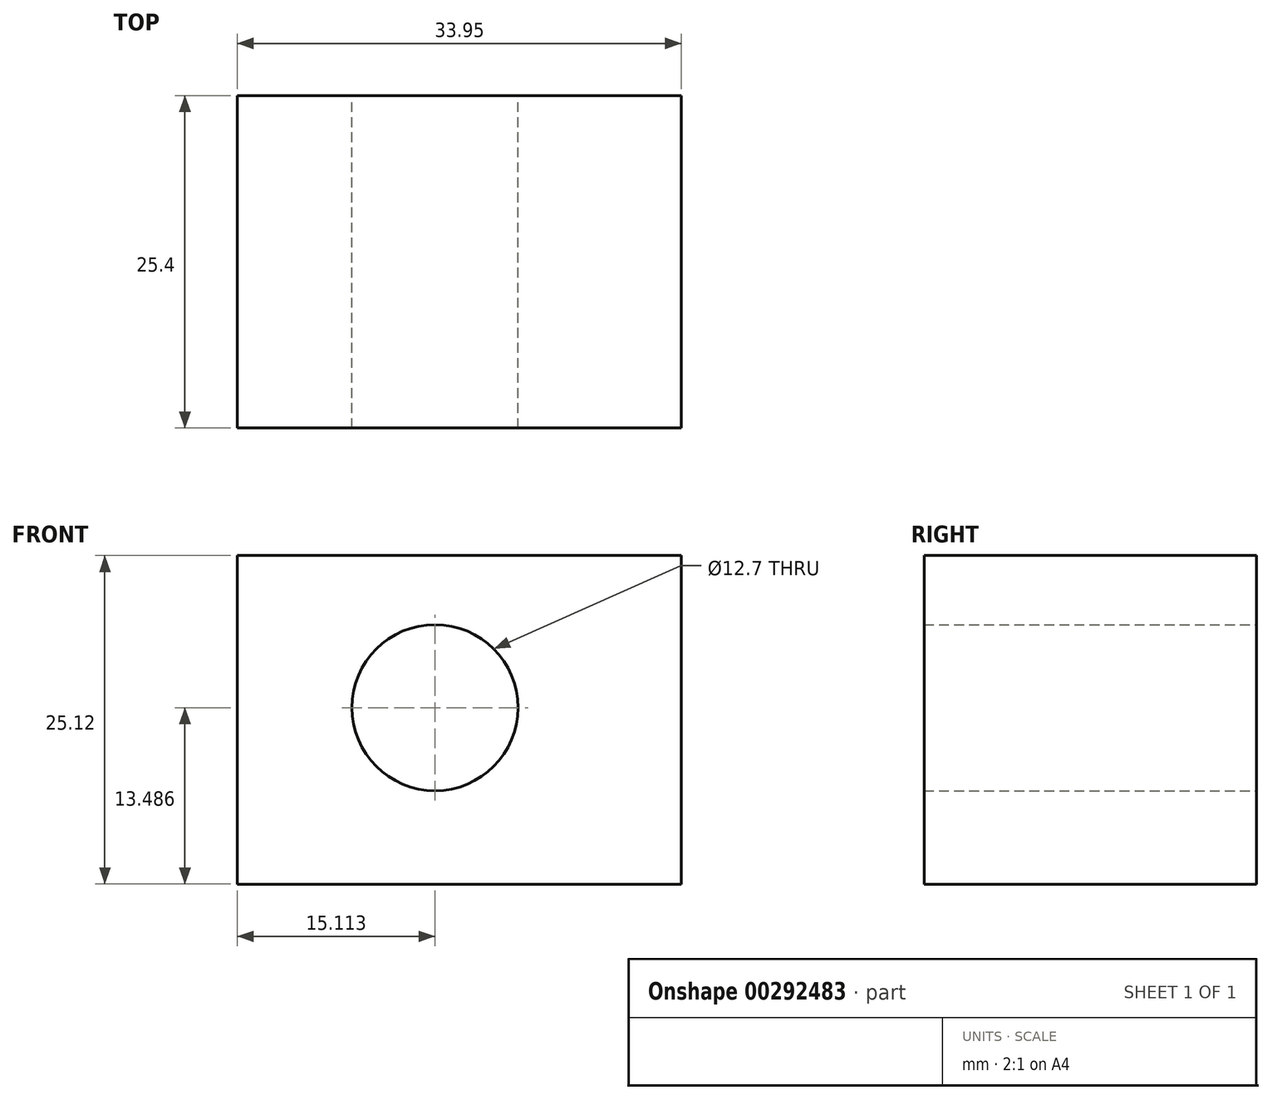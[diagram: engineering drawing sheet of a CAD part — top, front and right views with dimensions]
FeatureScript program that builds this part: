
annotation { "Feature Type Name" : "Feature", "Feature Type Description" : "" }
export const myFeature = defineFeature(function(context is Context, id is Id, definition is map)
    precondition{}
    {
        {
            var Q0;
            Q0=qCreatedBy(makeId("Front.planeOp"),FACE);
            var sketch = newSketch(context, id + "F0", { "sketchPlane" : qUnion([Q0])});
            skLineSegment(sketch, "E0.bottom", {"start": v(-46.28, 40) * mm, "end": v(-12.33, 40) * mm});
            skLineSegment(sketch, "E0.top", {"start": v(-46.28, 14.89) * mm, "end": v(-12.33, 14.89) * mm});
            skLineSegment(sketch, "E0.left", {"start": v(-46.28, 40) * mm, "end": v(-46.28, 14.89) * mm});
            skLineSegment(sketch, "E0.right", {"start": v(-12.33, 40) * mm, "end": v(-12.33, 14.89) * mm});
            skSolve(sketch);
        }
        {
            var Q0;
            Q0=makeQuery(id+"F0.imprint","IMPRINT",FACE,{"disambiguationData":[TD([[makeQuery(id+"F0.imprint","IMPRINT",EDGE,{"derivedFrom":sQuery(id+"F0.wireOp",EDGE,"E0.bottom")}),-1.0]])]});
            extrude(context, id + "F1", {"entities" : qUnion([Q0]), "depth" : 25.4 * mm});
        }
        {
            var Q0;
            Q0=makeQuery(id+"F1.opExtrude","CAP_FACE",FACE,{"disambiguationData":[OSD([sQuery(id+"F0.wireOp",EDGE,"E0.bottom"),sQuery(id+"F0.wireOp",EDGE,"E0.top"),sQuery(id+"F0.wireOp",EDGE,"E0.left"),sQuery(id+"F0.wireOp",EDGE,"E0.right")])],"isStart":false});
            var sketch = newSketch(context, id + "F2", { "sketchPlane" : qUnion([Q0])});
            skLineSegment(sketch, "E1.bottom", {"start": v(-31.17, 28.38) * mm, "end": v(-22.1, 28.38) * mm});
            skLineSegment(sketch, "E1.top", {"start": v(-31.17, 18.37) * mm, "end": v(-22.1, 18.37) * mm});
            skLineSegment(sketch, "E1.left", {"start": v(-31.17, 28.38) * mm, "end": v(-31.17, 18.37) * mm});
            skLineSegment(sketch, "E1.right", {"start": v(-22.1, 28.38) * mm, "end": v(-22.1, 18.37) * mm});
            skSolve(sketch);
        }
        {
            var Q0;
            Q0=sQuery(id+"F2.wireOp",VERTEX,"E1.left.start");
            var Q1;
            Q1=makeQuery(id+"F1.opExtrude","SWEPT_BODY",BODY,{"disambiguationData":[OSD([sQuery(id+"F0.wireOp",EDGE,"E0.bottom"),sQuery(id+"F0.wireOp",EDGE,"E0.top"),sQuery(id+"F0.wireOp",EDGE,"E0.left"),sQuery(id+"F0.wireOp",EDGE,"E0.right")])]});
            hole(context, id + "F3", {"style" : HoleStyle.SIMPLE, "endStyle" : HoleEndStyle.BLIND, "holeDiameter" : 12.7 * mm, "holeDepth" : 25.4 * mm, "tappedDepth" : 12.7 * mm, "tapClearance" : 3, "locations" : qUnion([Q0]), "scope" : qUnion([Q1])});
        }
    });
